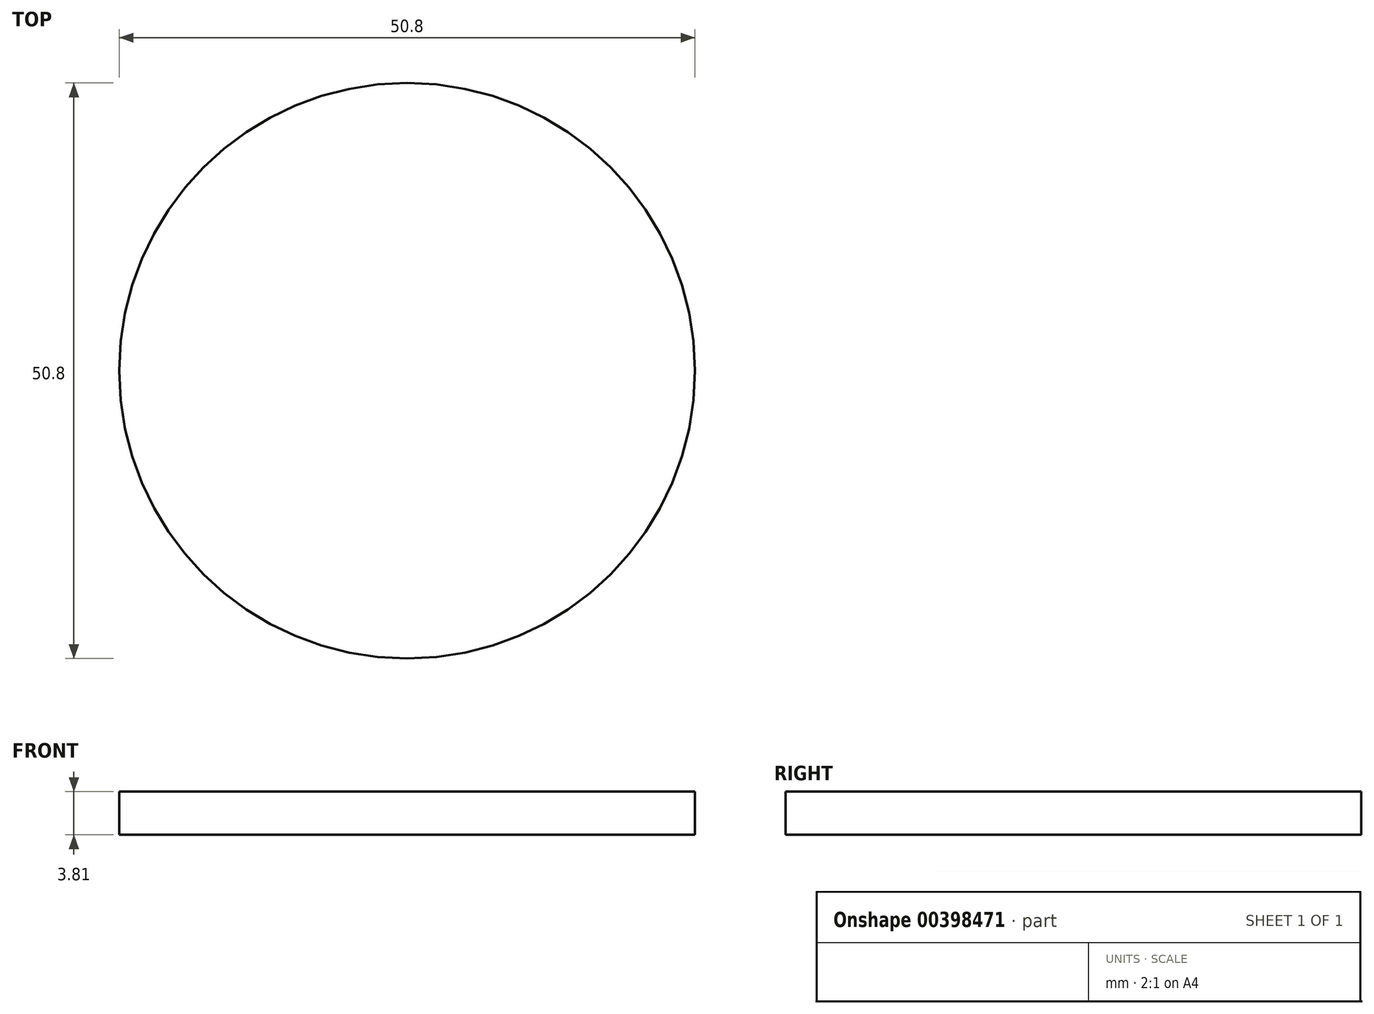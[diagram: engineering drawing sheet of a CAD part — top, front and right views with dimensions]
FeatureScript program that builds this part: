
annotation { "Feature Type Name" : "Feature", "Feature Type Description" : "" }
export const myFeature = defineFeature(function(context is Context, id is Id, definition is map)
    precondition{}
    {
        {
            var Q0;
            Q0=qCreatedBy(makeId("Top.planeOp"),FACE);
            var sketch = newSketch(context, id + "F0", { "sketchPlane" : qUnion([Q0])});
            skCircle(sketch, "E0", {"center": v(0, 0) * mm, "radius": 25.4 * mm});
            skSolve(sketch);
        }
        {
            var Q0;
            Q0=makeQuery(id+"F0.imprint","IMPRINT",FACE,{"disambiguationData":[TD([[makeQuery(id+"F0.imprint","IMPRINT",EDGE,{"derivedFrom":sQuery(id+"F0.wireOp",EDGE,"E0")}),1.0]])]});
            extrude(context, id + "F1", {"entities" : qUnion([Q0]), "depth" : 3.8 * mm});
        }
    });
